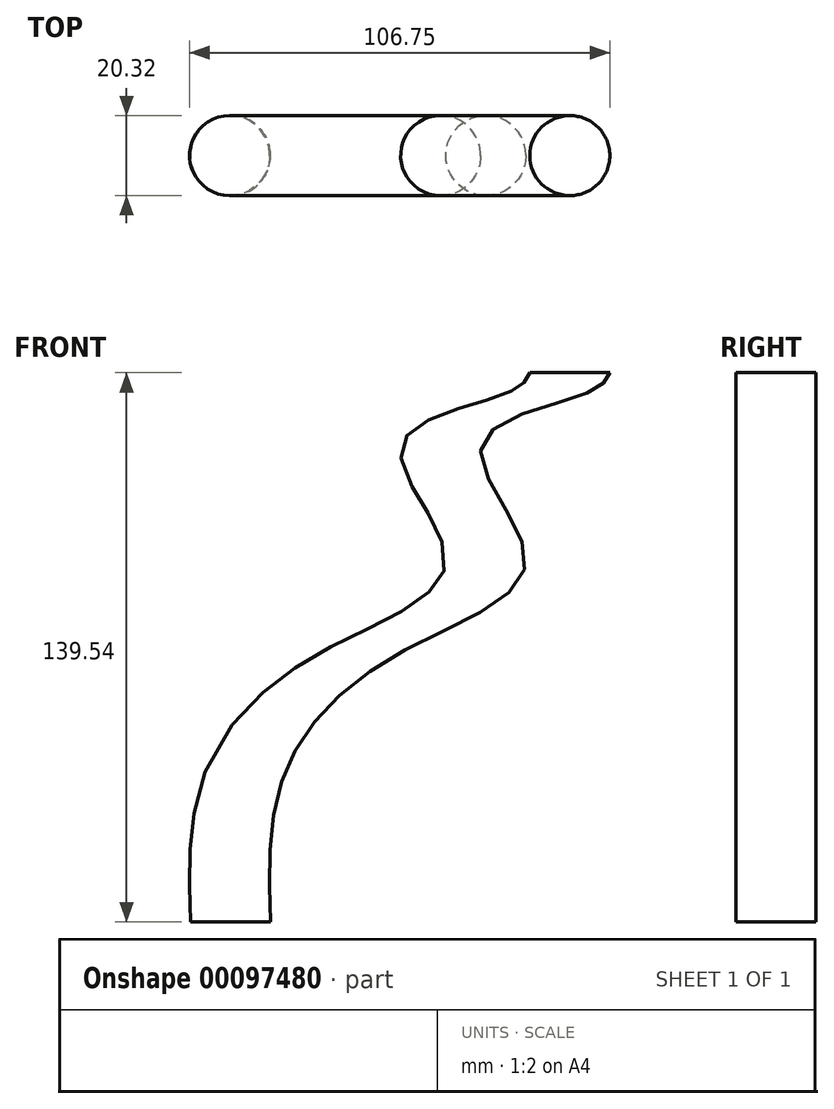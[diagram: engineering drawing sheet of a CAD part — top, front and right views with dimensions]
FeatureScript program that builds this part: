
annotation { "Feature Type Name" : "Feature", "Feature Type Description" : "" }
export const myFeature = defineFeature(function(context is Context, id is Id, definition is map)
    precondition{}
    {
        {
            var Q0;
            Q0=qCreatedBy(makeId("Top.planeOp"),FACE);
            var sketch = newSketch(context, id + "F0", { "sketchPlane" : qUnion([Q0])});
            skCircle(sketch, "E0", {"center": v(0, 0) * mm, "radius": 10.16 * mm});
            skSolve(sketch);
        }
        {
            var Q0;
            Q0=qCreatedBy(makeId("Front.planeOp"),FACE);
            var sketch = newSketch(context, id + "F1", { "sketchPlane" : qUnion([Q0])});
            skFitSpline(sketch, "E1", {"points": [v(0, 0) * mm, v(3.9, 38.55) * mm, v(33.7, 68.84) * mm, v(64.87, 91.72) * mm, v(53.69, 121.35) * mm, v(81.46, 134.79) * mm, v(86.2, 139.54) * mm], "startDerivative": vector(-6.3, 212.24) * mm, "endDerivative": vector(28.48, 61.73) * mm});
            skSolve(sketch);
        }
        {
            var Q0;
            Q0=makeQuery(id+"F0.imprint","IMPRINT",FACE,{"disambiguationData":[TD([[makeQuery(id+"F0.imprint","IMPRINT",EDGE,{"derivedFrom":sQuery(id+"F0.wireOp",EDGE,"E0")}),1.0]])]});
            var Q1;
            Q1=sQuery(id+"F1.wireOp",EDGE,"E1");
            sweep(context, id + "F2", {"profiles" : qUnion([Q0]), "path" : qUnion([Q1]), "keepProfileOrientation" : true});
        }
    });
